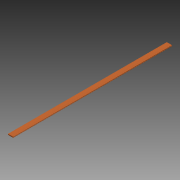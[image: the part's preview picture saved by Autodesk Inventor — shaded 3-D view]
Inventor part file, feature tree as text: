
AUTODESK INVENTOR PART (.ipt)
format: ipt  version: 2015 (Build 190159000, 159)  size: 93,184 bytes
history: native  units: in
note: dims shown in document units (in); Inventor stores cm internally (conversion verified against a paired STEP export)
features: extrude x1, sketch x1
ambient origin geometry x8: Origin, YZ Plane, XZ Plane, XY Plane, X Axis, Y Axis, Z Axis, Center Point
bodies: Solid1 (feature_tree)
feature tree (2):
  extrude  "Extrusion1"  Depth=0.94in
  sketch  "Sketch1"  dims[d0=5.36in d1=0.94in d3=0.25in d4=0.375in d5=0.125in d6=160.0in d7=0.0in]
